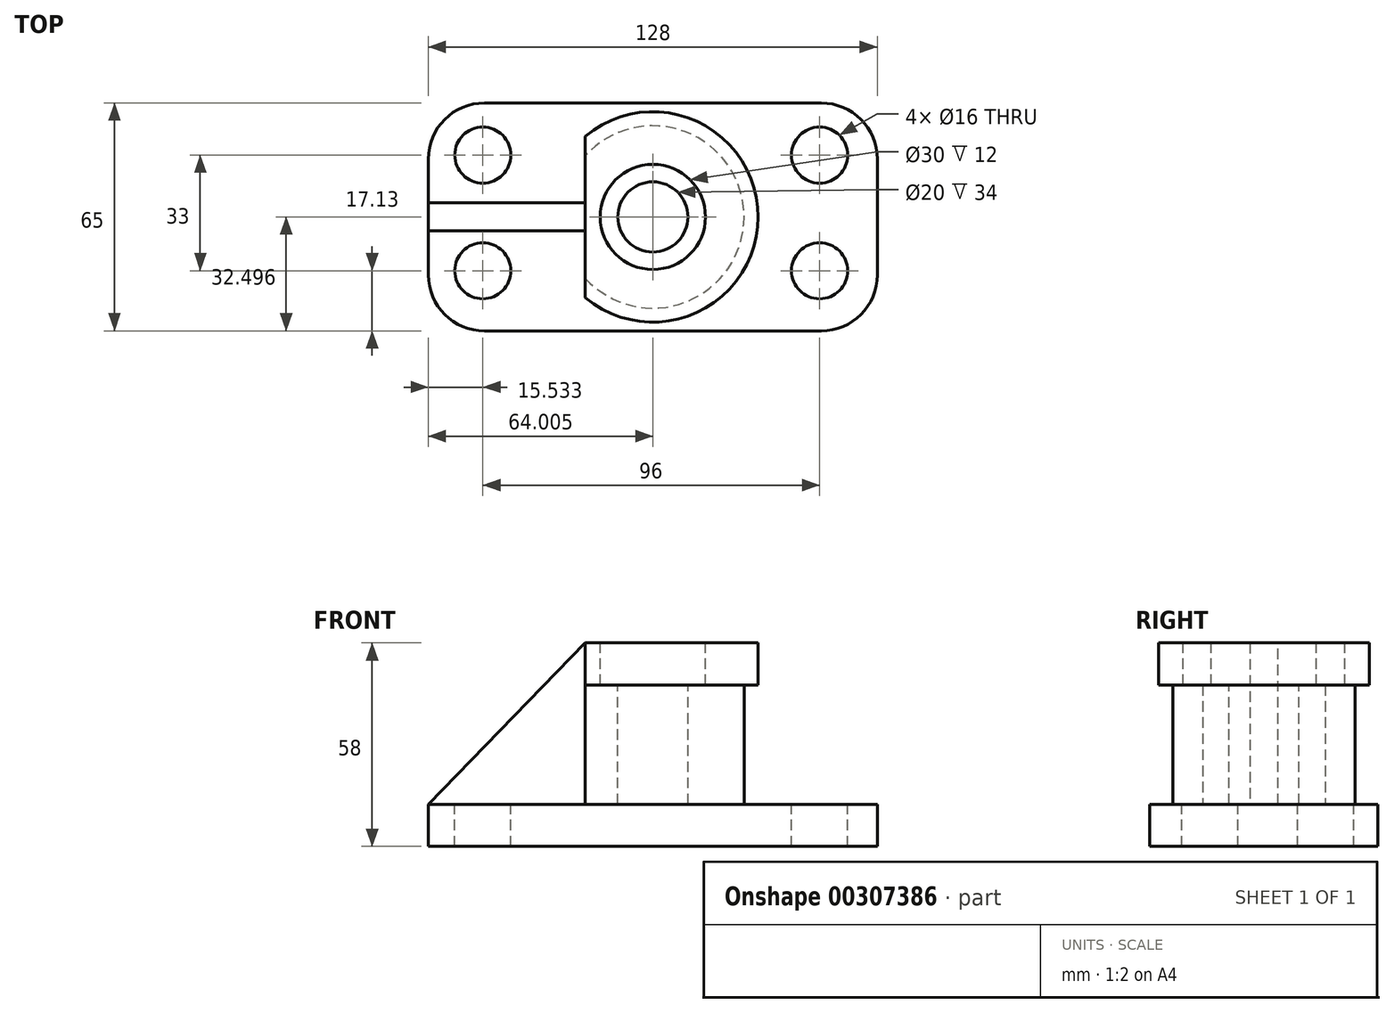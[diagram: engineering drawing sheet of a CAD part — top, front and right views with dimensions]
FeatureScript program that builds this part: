
annotation { "Feature Type Name" : "Feature", "Feature Type Description" : "" }
export const myFeature = defineFeature(function(context is Context, id is Id, definition is map)
    precondition{}
    {
        {
            var Q0;
            Q0=qCreatedBy(makeId("Top.planeOp"),FACE);
            var sketch = newSketch(context, id + "F0", { "sketchPlane" : qUnion([Q0])});
            skLineSegment(sketch, "E0.bottom", {"start": v(-38.32, -12.85) * mm, "end": v(57.68, -12.85) * mm});
            skLineSegment(sketch, "E0.top", {"start": v(-38.32, 52.15) * mm, "end": v(57.68, 52.15) * mm});
            skLineSegment(sketch, "E0.left", {"start": v(-54.32, 3.15) * mm, "end": v(-54.32, 36.15) * mm});
            skLineSegment(sketch, "E0.right", {"start": v(73.68, 3.15) * mm, "end": v(73.68, 36.15) * mm});
            skPoint(sketch, "E1.visualSharp", {"position": v(-54.32, 52.15) * mm});
            skArc(sketch, "E1.filletArc", {"start": v(-38.32, 52.15) * mm, "mid": v(-49.63, 47.46) * mm, "end": v(-54.32, 36.15) * mm});
            skPoint(sketch, "E2.visualSharp", {"position": v(-54.32, -12.85) * mm});
            skArc(sketch, "E2.filletArc", {"start": v(-54.32, 3.15) * mm, "mid": v(-49.63, -8.17) * mm, "end": v(-38.32, -12.85) * mm});
            skPoint(sketch, "E3.visualSharp", {"position": v(73.68, -12.85) * mm});
            skArc(sketch, "E3.filletArc", {"start": v(57.68, -12.85) * mm, "mid": v(69, -8.17) * mm, "end": v(73.68, 3.15) * mm});
            skPoint(sketch, "E4.visualSharp", {"position": v(73.68, 52.15) * mm});
            skArc(sketch, "E4.filletArc", {"start": v(73.68, 36.15) * mm, "mid": v(69, 47.46) * mm, "end": v(57.68, 52.15) * mm});
            skSolve(sketch);
        }
        {
            var Q0;
            Q0 = qSketchRegion(id + "F0", true);
            extrude(context, id + "F1", {"entities" : qUnion([Q0]), "depth" : 12 * mm});
        }
        {
            var Q0;
            Q0=makeQuery(id+"F1.opExtrude","CAP_FACE",FACE,{"disambiguationData":[OSD([sQuery(id+"F0.wireOp",EDGE,"E0.bottom"),sQuery(id+"F0.wireOp",EDGE,"E0.top"),sQuery(id+"F0.wireOp",EDGE,"E0.left"),sQuery(id+"F0.wireOp",EDGE,"E0.right"),sQuery(id+"F0.wireOp",EDGE,"E1.filletArc"),sQuery(id+"F0.wireOp",EDGE,"E2.filletArc"),sQuery(id+"F0.wireOp",EDGE,"E3.filletArc"),sQuery(id+"F0.wireOp",EDGE,"E4.filletArc")])],"isStart":false});
            var sketch = newSketch(context, id + "F2", { "sketchPlane" : qUnion([Q0])});
            skCircle(sketch, "E5", {"center": v(-38.79, 37.28) * mm, "radius": 8 * mm});
            skCircle(sketch, "E6", {"center": v(-38.79, 4.28) * mm, "radius": 8 * mm});
            skCircle(sketch, "E7", {"center": v(57.21, 37.28) * mm, "radius": 8 * mm});
            skCircle(sketch, "E8", {"center": v(57.21, 4.28) * mm, "radius": 8 * mm});
            skLineSegment(sketch, "E9", {"start": v(-54.32, 19.65) * mm, "end": v(73.68, 19.65) * mm, "construction": true});
            skLineSegment(sketch, "E10", {"start": v(9.68, -12.85) * mm, "end": v(9.68, 52.15) * mm, "construction": true});
            skSolve(sketch);
        }
        {
            var Q0;
            Q0=makeQuery(id+"F2.imprint","IMPRINT",FACE,{"disambiguationData":[TD([[makeQuery(id+"F2.imprint","IMPRINT",EDGE,{"derivedFrom":sQuery(id+"F2.wireOp",EDGE,"E5")}),1.0]])]});
            var Q1;
            Q1=makeQuery(id+"F2.imprint","IMPRINT",FACE,{"disambiguationData":[TD([[makeQuery(id+"F2.imprint","IMPRINT",EDGE,{"derivedFrom":sQuery(id+"F2.wireOp",EDGE,"E6")}),1.0]])]});
            var Q2;
            Q2=makeQuery(id+"F2.imprint","IMPRINT",FACE,{"disambiguationData":[TD([[makeQuery(id+"F2.imprint","IMPRINT",EDGE,{"derivedFrom":sQuery(id+"F2.wireOp",EDGE,"E8")}),1.0]])]});
            var Q3;
            Q3=makeQuery(id+"F2.imprint","IMPRINT",FACE,{"disambiguationData":[TD([[makeQuery(id+"F2.imprint","IMPRINT",EDGE,{"derivedFrom":sQuery(id+"F2.wireOp",EDGE,"E7")}),1.0]])]});
            extrude(context, id + "F3", {"entities" : qUnion([Q0, Q1, Q2, Q3]), "operationType" : NewBodyOperationType.REMOVE, "oppositeDirection" : true, "depth" : 12 * mm});
        }
        {
            var Q0;
            Q0=makeQuery(id+"F1.opExtrude","CAP_FACE",FACE,{"disambiguationData":[OSD([sQuery(id+"F0.wireOp",EDGE,"E0.bottom"),sQuery(id+"F0.wireOp",EDGE,"E0.top"),sQuery(id+"F0.wireOp",EDGE,"E0.left"),sQuery(id+"F0.wireOp",EDGE,"E0.right"),sQuery(id+"F0.wireOp",EDGE,"E1.filletArc"),sQuery(id+"F0.wireOp",EDGE,"E2.filletArc"),sQuery(id+"F0.wireOp",EDGE,"E3.filletArc"),sQuery(id+"F0.wireOp",EDGE,"E4.filletArc")])],"isStart":false});
            var sketch = newSketch(context, id + "F4", { "sketchPlane" : qUnion([Q0])});
            skLineSegment(sketch, "E11", {"start": v(9.68, 52.15) * mm, "end": v(9.68, -12.85) * mm, "construction": true});
            skLineSegment(sketch, "E12", {"start": v(-54.32, 19.65) * mm, "end": v(73.68, 19.65) * mm, "construction": true});
            skCircle(sketch, "E13", {"center": v(9.68, 19.65) * mm, "radius": 26 * mm});
            skSolve(sketch);
        }
        {
            var Q0;
            Q0=makeQuery(id+"F4.imprint","IMPRINT",FACE,{"disambiguationData":[TD([[makeQuery(id+"F4.imprint","IMPRINT",EDGE,{"derivedFrom":sQuery(id+"F4.wireOp",EDGE,"E13")}),1.0]])]});
            extrude(context, id + "F5", {"entities" : qUnion([Q0]), "operationType" : NewBodyOperationType.ADD, "depth" : 46 * mm});
        }
        {
            var Q0;
            Q0=makeQuery(id+"F5.opExtrude","CAP_FACE",FACE,{"disambiguationData":[OSD([sQuery(id+"F4.wireOp",EDGE,"E13")])],"isStart":false});
            var sketch = newSketch(context, id + "F6", { "sketchPlane" : qUnion([Q0])});
            skCircle(sketch, "E14", {"center": v(9.68, 19.65) * mm, "radius": 15 * mm});
            skSolve(sketch);
        }
        {
            var Q0;
            Q0=makeQuery(id+"F6.imprint","IMPRINT",FACE,{"disambiguationData":[TD([[makeQuery(id+"F6.imprint","IMPRINT",EDGE,{"derivedFrom":sQuery(id+"F6.wireOp",EDGE,"E14")}),1.0]])]});
            extrude(context, id + "F7", {"entities" : qUnion([Q0]), "operationType" : NewBodyOperationType.REMOVE, "oppositeDirection" : true, "depth" : 12 * mm});
        }
        {
            var Q0;
            Q0=makeQuery(id+"F7.boolean.opBoolean","COPY",FACE,{"derivedFrom":makeQuery(id+"F7.opExtrude","CAP_FACE",FACE,{"disambiguationData":[OSD([sQuery(id+"F6.wireOp",EDGE,"E14")])],"isStart":false})});
            var sketch = newSketch(context, id + "F8", { "sketchPlane" : qUnion([Q0])});
            skCircle(sketch, "E15", {"center": v(9.68, 19.65) * mm, "radius": 10 * mm});
            skSolve(sketch);
        }
        {
            var Q0;
            Q0=makeQuery(id+"F8.imprint","IMPRINT",FACE,{"disambiguationData":[TD([[makeQuery(id+"F8.imprint","IMPRINT",EDGE,{"derivedFrom":sQuery(id+"F8.wireOp",EDGE,"E15")}),1.0]])]});
            extrude(context, id + "F9", {"entities" : qUnion([Q0]), "operationType" : NewBodyOperationType.REMOVE, "oppositeDirection" : true, "depth" : 34 * mm});
        }
        {
            var Q0;
            Q0=makeQuery(id+"F5.opExtrude","CAP_FACE",FACE,{"disambiguationData":[OSD([sQuery(id+"F4.wireOp",EDGE,"E13")])],"isStart":false});
            var sketch = newSketch(context, id + "F10", { "sketchPlane" : qUnion([Q0])});
            skCircle(sketch, "E16", {"center": v(9.68, 19.65) * mm, "radius": 30 * mm});
            skSolve(sketch);
        }
        {
            var Q0;
            Q0=makeQuery(id+"F10.imprint","IMPRINT",FACE,{"disambiguationData":[TD([[makeQuery(id+"F10.imprint","IMPRINT",EDGE,{"derivedFrom":sQuery(id+"F10.wireOp",EDGE,"E16")}),1.0]])]});
            extrude(context, id + "F11", {"entities" : qUnion([Q0]), "operationType" : NewBodyOperationType.ADD, "oppositeDirection" : true, "depth" : 12 * mm});
        }
        {
            var Q0;
            {var subQ0=sQuery(id+"F4.wireOp",EDGE,"E13");Q0=makeQuery(id+"F11.boolean.opBoolean","MERGE",FACE,{"derivedFrom":[makeQuery(id+"F5.opExtrude","CAP_FACE",FACE,{"disambiguationData":[OSD([subQ0])],"isStart":false}),makeQuery(id+"F11.opExtrude","CAP_FACE",FACE,{"disambiguationData":[OSD([subQ0,sQuery(id+"F10.wireOp",EDGE,"E16")])],"isStart":true})]});}
            var sketch = newSketch(context, id + "F12", { "sketchPlane" : qUnion([Q0])});
            skLineSegment(sketch, "E17", {"start": v(-9.55, 42.67) * mm, "end": v(-9.55, -3.38) * mm});
            skSolve(sketch);
        }
        {
            var Q0;
            {var subQ0=sQuery(id+"F12.wireOp",EDGE,"E17");Q0=makeQuery(id+"F12.imprint","IMPRINT",FACE,{"disambiguationData":[TD([[makeQuery(id+"F12.imprint","IMPRINT",EDGE,{"derivedFrom":subQ0}),-1.0]])]});}
            extrude(context, id + "F13", {"entities" : qUnion([Q0]), "operationType" : NewBodyOperationType.REMOVE, "oppositeDirection" : true, "depth" : 46 * mm});
        }
        {
            var Q0;
            Q0=makeQuery(id+"F13.boolean.opBoolean","MERGE",FACE,{"derivedFrom":[makeQuery(id+"F1.opExtrude","CAP_FACE",FACE,{"disambiguationData":[OSD([sQuery(id+"F0.wireOp",EDGE,"E0.bottom"),sQuery(id+"F0.wireOp",EDGE,"E0.top"),sQuery(id+"F0.wireOp",EDGE,"E0.left"),sQuery(id+"F0.wireOp",EDGE,"E0.right"),sQuery(id+"F0.wireOp",EDGE,"E1.filletArc"),sQuery(id+"F0.wireOp",EDGE,"E2.filletArc"),sQuery(id+"F0.wireOp",EDGE,"E3.filletArc"),sQuery(id+"F0.wireOp",EDGE,"E4.filletArc")])],"isStart":false}),makeQuery(id+"F13.opExtrude","CAP_FACE",FACE,{"disambiguationData":[OSD([sQuery(id+"F10.wireOp",EDGE,"E16"),sQuery(id+"F12.wireOp",EDGE,"E17")])],"isStart":false})]});
            var sketch = newSketch(context, id + "F14", { "sketchPlane" : qUnion([Q0])});
            skLineSegment(sketch, "E18", {"start": v(-54.32, 19.65) * mm, "end": v(-9.55, 19.65) * mm, "construction": true});
            skLineSegment(sketch, "E19", {"start": v(-54.32, 15.65) * mm, "end": v(-9.55, 15.65) * mm});
            skLineSegment(sketch, "E20", {"start": v(-54.32, 23.65) * mm, "end": v(-9.55, 23.65) * mm});
            skSolve(sketch);
        }
        {
            var Q0;
            {var subQ0=sQuery(id+"F14.wireOp",EDGE,"E19");Q0=makeQuery(id+"F14.imprint","IMPRINT",FACE,{"disambiguationData":[TD([[makeQuery(id+"F14.imprint","IMPRINT",EDGE,{"derivedFrom":subQ0}),1.0]])]});}
            extrude(context, id + "F15", {"entities" : qUnion([Q0]), "operationType" : NewBodyOperationType.ADD, "depth" : 46 * mm});
        }
        {
            var Q0;
            Q0=makeQuery(id+"F15.opExtrude","SWEPT_FACE",FACE,{"disambiguationData":[OSD([sQuery(id+"F14.wireOp",EDGE,"E19")])]});
            var sketch = newSketch(context, id + "F16", { "sketchPlane" : qUnion([Q0])});
            skLineSegment(sketch, "E21", {"start": v(-9.55, 58) * mm, "end": v(-54.32, 12) * mm});
            skLineSegment(sketch, "E22", {"start": v(-54.32, 12) * mm, "end": v(-9.55, 12) * mm});
            skLineSegment(sketch, "E23", {"start": v(-9.55, 12) * mm, "end": v(-9.55, 58) * mm});
            skSolve(sketch);
        }
        {
            var Q0;
            Q0=makeQuery(id+"F16.imprint","IMPRINT",FACE,{"disambiguationData":[TD([[makeQuery(id+"F16.imprint","IMPRINT",EDGE,{"derivedFrom":sQuery(id+"F16.wireOp",EDGE,"E21")}),-1.0]])]});
            extrude(context, id + "F17", {"entities" : qUnion([Q0]), "operationType" : NewBodyOperationType.REMOVE, "oppositeDirection" : true, "depth" : 25 * mm});
        }
    });
